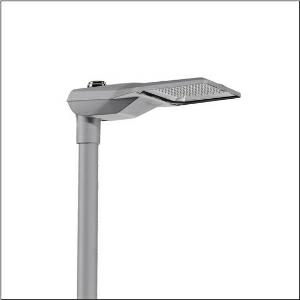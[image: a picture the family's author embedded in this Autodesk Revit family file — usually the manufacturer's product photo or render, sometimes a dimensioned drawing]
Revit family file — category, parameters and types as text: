
# Revit family: streetlight_sl_21_midi___pl52_5xe7h37n08mb_03fc
name_source: partatom
category: Lighting Fixtures
units: mm (PartAtom-declared; Revit-internal decimal feet)

## family parameters
Cut with Voids When Loaded = No
Host = Face
Light Source = No
Part Type = Normal
Room Calculation Point = No
Round Connector Dimension = Use Diameter
Shared = No

## types (1)
- --- (1 x LED, 17960 lm, 136 W, 3000K)
    Apparent Load = 136 VA
    CIE Flux Codes = 27 59 98 100 100
    Color Rendering = 70
    Color Temperature = 3000K
    Default Elevation = 1800 mm
    Description = Streetlight SL 21 midi, mast luminaire, primary light control with lens, of PMMA, primary optical cover: cover, of toughened safety glass, transparent, light distribution: PL52, light emission: direct distribution, primary light characteristic: asymmetric, installation type: side-entry, LED, 3G 2.5mm², High Power LED, rated luminous flux: 17.960lm, luminous efficacy: 132lm/W, light colour: 730, colour temperature: 3000K, control gear: NEMA (7pin), control: overheat protection, pre-setting: linear dimming characteristic, constant luminous flux control, time-dependent luminous flux control, flexible luminous flux parameterisation, mains connection: 220..240V, AC, 50/60Hz, connection cable pre-assembled, cable length: 12,5m, wiring characteristics: H05VV-F, start of lifetime: 136W, end of service life: 142W, reduction: 61W, luminaire housing, of diecast aluminium (EN AC-44300), powder-coated, SITECO metallic grey (DB 702S), corrosivity category C5 high according to DIN EN ISO 12944, multi-level sealing system, sealing non-destructively replaceable, inclination adjustable: 0°, 5°, 10°, 15°, length: 644mm, width: 335mm, height: 110mm, spigot size: 42mm (side-entry), mounting height: 4..8m, protection rating (complete): IP66, insulation class (complete): insulation class I (protective earthing), certification: CE, ENEC, ENEC+, VDE, impact resistance: IK10, permissible operating ambient temperature for outdoor applications: -40..+50°C, standard-compliant lighting for roads and squares, packaging unit: 1 piece

Light Distribution: PL52
    Height = 111 mm
    Lamp = 1 x LED
    Lamp Light Flux = 17960 lm
    Lamp Power = 136 W
    Lamp count = 1
    Length = 644 mm
    Luminous efficacy = 132 lm/W
    Manufacturer = Siteco
    ModVariant = No
    Model = 5XE7H37N08MB
    Number of Poles = 1
    OnlyDefault = Yes
    Power Factor = 1
    Product Name = Streetlight SL 21 midi | PL52
    Product group = mast luminaire | pylon top
    ProductGroupID = 6100
    Protection Class = Protection class I
    Protection Degree = IP 66
    RLX_Detail_Level = 1
    RLX_Emergency_Light_Flux = 0 lm
    RLX_Emergency_Type = 0
    RLX_Emergency_Type_DB = No
    RlxData = <blob elided: 36149 chars, md5=dfe4ee0a>
    Socket = socket
    Standby Power = 0 W
    System Light Flux = 17960 lm
    System Power = 136 W
    Type Comments = factory setting: luminous flux: 100 % | dim-lin: 254 | 695 mA
    Type Image = l_1294377.jpg
    URL = http://relux.com
    VarID = @adj_136383
    Voltage = 0 V
    Weight = 0.00 kg
    Width = 336 mm

## geometry (parser evidence)
native form markers: Blend x4, Sweep x9
no freeform markers — native parametric forms only
